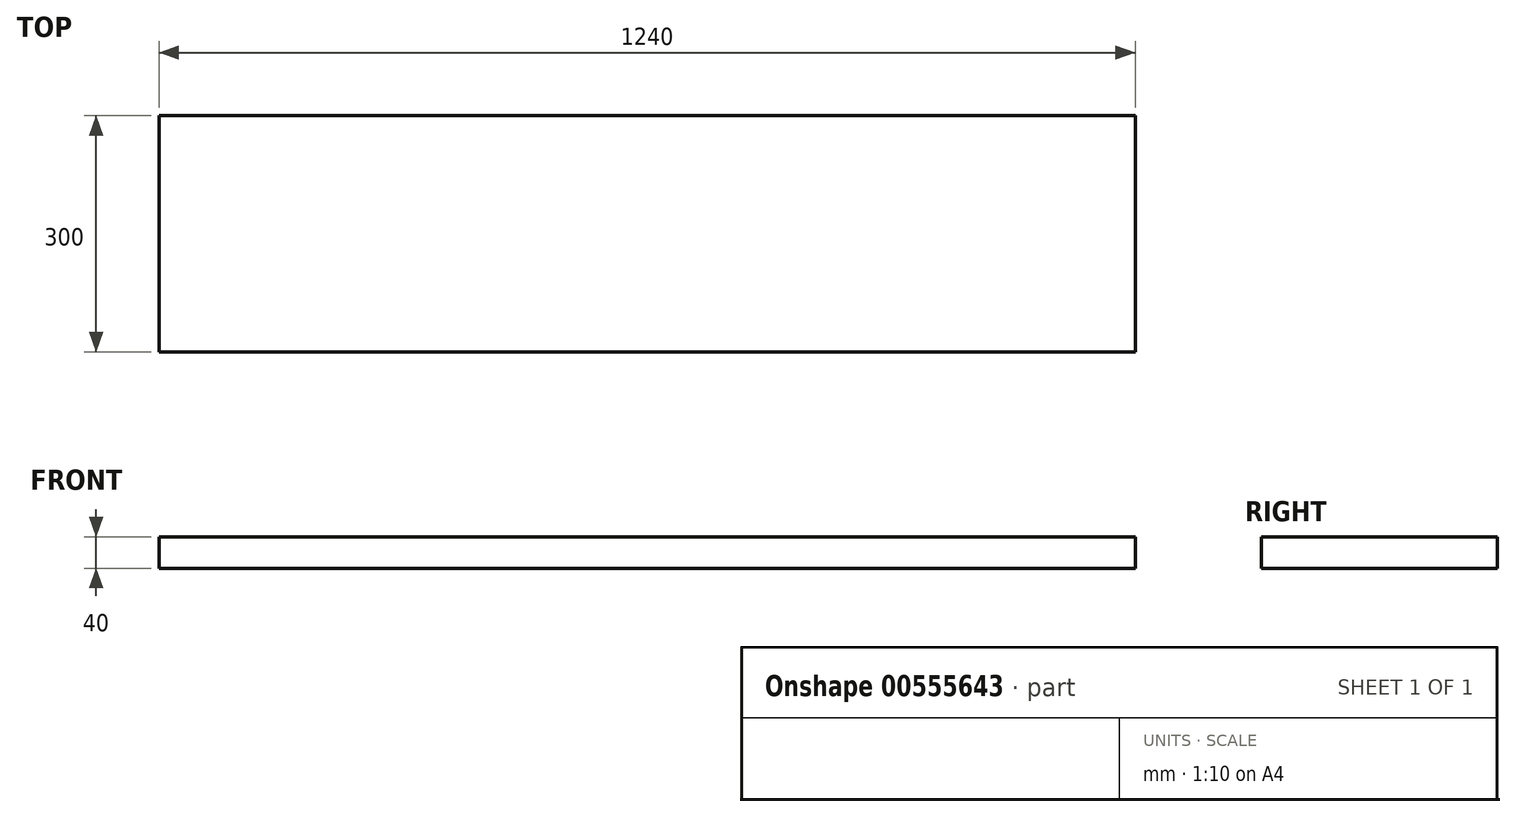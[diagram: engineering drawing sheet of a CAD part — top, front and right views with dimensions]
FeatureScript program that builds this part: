
annotation { "Feature Type Name" : "Feature", "Feature Type Description" : "" }
export const myFeature = defineFeature(function(context is Context, id is Id, definition is map)
    precondition{}
    {
        {
            var Q0;
            Q0=qCreatedBy(makeId("Top.planeOp"),FACE);
            var sketch = newSketch(context, id + "F0", { "sketchPlane" : qUnion([Q0])});
            skLineSegment(sketch, "E0.bottom", {"start": v(620, -150) * mm, "end": v(-620, -150) * mm});
            skLineSegment(sketch, "E0.top", {"start": v(620, 150) * mm, "end": v(-620, 150) * mm});
            skLineSegment(sketch, "E0.left", {"start": v(620, -150) * mm, "end": v(620, 150) * mm});
            skLineSegment(sketch, "E0.right", {"start": v(-620, -150) * mm, "end": v(-620, 150) * mm});
            skPoint(sketch, "E0.middle", {"position": v(0, 0) * mm});
            skSolve(sketch);
        }
        {
            var Q0;
            Q0 = qSketchRegion(id + "F0", true);
            extrude(context, id + "F1", {"entities" : qUnion([Q0]), "depth" : 40 * mm, "offsetDistance" : 25 * mm});
        }
    });
